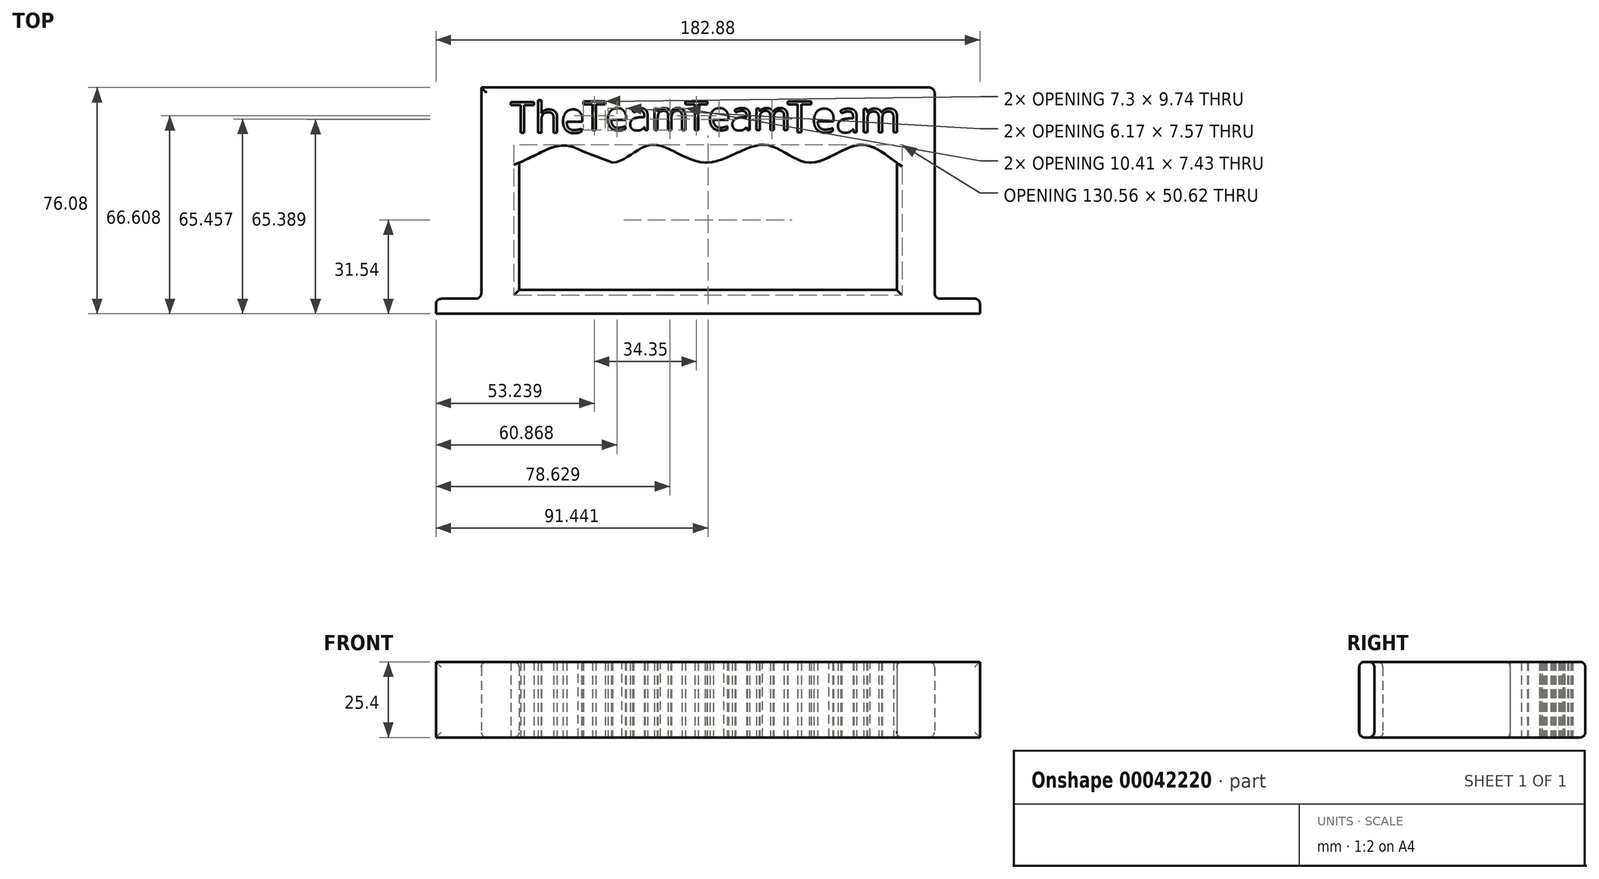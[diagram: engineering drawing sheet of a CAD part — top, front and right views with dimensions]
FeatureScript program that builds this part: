
annotation { "Feature Type Name" : "Feature", "Feature Type Description" : "" }
export const myFeature = defineFeature(function(context is Context, id is Id, definition is map)
    precondition{}
    {
        {
            var Q0;
            Q0=qCreatedBy(makeId("Top.planeOp"),FACE);
            var sketch = newSketch(context, id + "F0", { "sketchPlane" : qUnion([Q0])});
            skLineSegment(sketch, "E0", {"start": v(-62.58, -21.01) * mm, "end": v(64.42, -21.01) * mm});
            skLineSegment(sketch, "E1", {"start": v(-62.58, -21.01) * mm, "end": v(-62.58, 29.79) * mm});
            skLineSegment(sketch, "E2", {"start": v(64.42, -21.01) * mm, "end": v(64.42, 29.79) * mm});
            skLineSegment(sketch, "E3", {"start": v(-32.01, 29.79) * mm, "end": v(-31.1, 29.79) * mm});
            skLineSegment(sketch, "E4", {"start": v(-62.58, 29.79) * mm, "end": v(-62.58, 55.07) * mm});
            skLineSegment(sketch, "E5", {"start": v(-62.58, 55.07) * mm, "end": v(64.42, 55.07) * mm});
            skLineSegment(sketch, "E6", {"start": v(64.42, 55.07) * mm, "end": v(64.42, 29.79) * mm});
            skLineSegment(sketch, "E7", {"start": v(-46.2, 35.5) * mm, "end": v(-31.1, 29.79) * mm});
            skFitSpline(sketch, "E8", {"points": [v(-62.58, 29.79) * mm, v(-46.2, 35.5) * mm, v(-31.1, 29.79) * mm, v(-17.79, 35.81) * mm, v(0, 29.79) * mm, v(19.89, 35.81) * mm, v(35.06, 29.79) * mm, v(51.91, 35.81) * mm, v(64.42, 29.79) * mm], "startDerivative": vector(149.24, 59.6) * mm, "endDerivative": vector(104.83, -72.99) * mm});
            skLineSegment(sketch, "E9.trimOffspring", {"start": v(0, 29.79) * mm, "end": v(0.55, 29.79) * mm});
            skLineSegment(sketch, "E10.trimOffspring", {"start": v(35.06, 29.79) * mm, "end": v(35.59, 29.79) * mm});
            skLineSegment(sketch, "E11", {"start": v(-62.58, 55.07) * mm, "end": v(-75.28, 55.07) * mm});
            skLineSegment(sketch, "E12", {"start": v(-75.28, 55.07) * mm, "end": v(-75.28, -21.01) * mm});
            skLineSegment(sketch, "E13", {"start": v(-75.28, -21.01) * mm, "end": v(-62.58, -21.01) * mm});
            skLineSegment(sketch, "E14", {"start": v(64.42, 55.07) * mm, "end": v(77.12, 55.07) * mm});
            skLineSegment(sketch, "E15", {"start": v(77.12, 55.07) * mm, "end": v(77.12, -20.98) * mm});
            skLineSegment(sketch, "E16", {"start": v(77.12, -20.98) * mm, "end": v(64.42, -21.01) * mm});
            skLineSegment(sketch, "E17", {"start": v(-62.58, -13) * mm, "end": v(64.42, -13) * mm});
            skLineSegment(sketch, "E18", {"start": v(-75.28, -21.01) * mm, "end": v(-90.52, -21.01) * mm});
            skLineSegment(sketch, "E19", {"start": v(-90.52, -21.01) * mm, "end": v(-90.52, -15.93) * mm});
            skLineSegment(sketch, "E20", {"start": v(-90.52, -15.93) * mm, "end": v(-75.28, -15.93) * mm});
            skLineSegment(sketch, "E21", {"start": v(77.12, -20.98) * mm, "end": v(92.36, -20.98) * mm});
            skLineSegment(sketch, "E22", {"start": v(92.36, -20.98) * mm, "end": v(92.36, -15.9) * mm});
            skLineSegment(sketch, "E23", {"start": v(92.36, -15.9) * mm, "end": v(77.12, -15.9) * mm});
            skText(sketch, "E24", { "text": "The", "fontName": "OpenSans-Regular.ttf"});
            skText(sketch, "E25", { "text": "Team\n", "fontName": "OpenSans-Regular.ttf"});
            skText(sketch, "E26", { "text": "Team", "fontName": "OpenSans-Regular.ttf"});
            skText(sketch, "E27", { "text": "Team", "fontName": "OpenSans-Regular.ttf"});
            const initialGuessF0  = {"E24": [-0.06546, 0.03985, 1, 0, 0.0104], "E25": [-0.04105, 0.04073, 1, 0, 0.00982], "E26": [-0.0067, 0.04073, 1, 0, 0.00982], "E27": [0.02766, 0.04002, 1, 0, 0.01053]};
            skSetInitialGuess(sketch, initialGuessF0);
            skSolve(sketch);
        }
        {
            var Q0;
            Q0 = qSketchRegion(id + "F0", true);
            extrude(context, id + "F1", {"entities" : qUnion([Q0]), "depth" : 25.4 * mm});
        }
        {
            var Q0;
            Q0=makeQuery(id+"F1.opExtrude","CAP_EDGE",EDGE,{"disambiguationData":[OSD([sQuery(id+"F0.wireOp",EDGE,"E5"),sQuery(id+"F0.wireOp",EDGE,"E11"),sQuery(id+"F0.wireOp",EDGE,"E14")])],"isStart":false});
            var Q1;
            Q1=makeQuery(id+"F1.opExtrude","CAP_EDGE",EDGE,{"disambiguationData":[OSD([sQuery(id+"F0.wireOp",EDGE,"E12")])],"isStart":false});
            var Q2;
            Q2=makeQuery(id+"F1.opExtrude","CAP_EDGE",EDGE,{"disambiguationData":[OSD([sQuery(id+"F0.wireOp",EDGE,"E20")])],"isStart":false});
            var Q3;
            Q3=makeQuery(id+"F1.opExtrude","CAP_EDGE",EDGE,{"disambiguationData":[OSD([sQuery(id+"F0.wireOp",EDGE,"E15")])],"isStart":false});
            var Q4;
            Q4=makeQuery(id+"F1.opExtrude","CAP_EDGE",EDGE,{"disambiguationData":[OSD([sQuery(id+"F0.wireOp",EDGE,"E23")])],"isStart":false});
            var Q5;
            Q5=makeQuery(id+"F1.opExtrude","SWEPT_EDGE",EDGE,{"disambiguationData":[OSD([sQuery(id+"F0.wireOp",EDGE,"E22"),sQuery(id+"F0.wireOp",EDGE,"E23")])]});
            var Q6;
            Q6=makeQuery(id+"F1.opExtrude","CAP_EDGE",EDGE,{"disambiguationData":[OSD([sQuery(id+"F0.wireOp",EDGE,"E23")])],"isStart":true});
            var Q7;
            Q7=makeQuery(id+"F1.opExtrude","SWEPT_EDGE",EDGE,{"disambiguationData":[OSD([sQuery(id+"F0.wireOp",EDGE,"E15"),sQuery(id+"F0.wireOp",EDGE,"E23")])]});
            var Q8;
            Q8=makeQuery(id+"F1.opExtrude","SWEPT_EDGE",EDGE,{"disambiguationData":[OSD([sQuery(id+"F0.wireOp",EDGE,"E14"),sQuery(id+"F0.wireOp",EDGE,"E15")])]});
            var Q9;
            Q9=makeQuery(id+"F1.opExtrude","CAP_EDGE",EDGE,{"disambiguationData":[OSD([sQuery(id+"F0.wireOp",EDGE,"E5"),sQuery(id+"F0.wireOp",EDGE,"E11"),sQuery(id+"F0.wireOp",EDGE,"E14")])],"isStart":true});
            var Q10;
            Q10=makeQuery(id+"F1.opExtrude","CAP_EDGE",EDGE,{"disambiguationData":[OSD([sQuery(id+"F0.wireOp",EDGE,"E17")])],"isStart":true});
            var Q11;
            Q11=makeQuery(id+"F1.opExtrude","CAP_EDGE",EDGE,{"disambiguationData":[OSD([sQuery(id+"F0.wireOp",EDGE,"E2")])],"isStart":true});
            var Q12;
            Q12=makeQuery(id+"F1.opExtrude","SWEPT_EDGE",EDGE,{"disambiguationData":[OSD([sQuery(id+"F0.wireOp",EDGE,"E19"),sQuery(id+"F0.wireOp",EDGE,"E20")])]});
            var Q13;
            Q13=makeQuery(id+"F1.opExtrude","SWEPT_EDGE",EDGE,{"disambiguationData":[OSD([sQuery(id+"F0.wireOp",EDGE,"E12"),sQuery(id+"F0.wireOp",EDGE,"E20")])]});
            var Q14;
            Q14=makeQuery(id+"F1.opExtrude","CAP_EDGE",EDGE,{"disambiguationData":[OSD([sQuery(id+"F0.wireOp",EDGE,"E20")])],"isStart":true});
            var Q15;
            Q15=makeQuery(id+"F1.opExtrude","CAP_EDGE",EDGE,{"disambiguationData":[OSD([sQuery(id+"F0.wireOp",EDGE,"E15")])],"isStart":true});
            var Q16;
            Q16=makeQuery(id+"F1.opExtrude","CAP_EDGE",EDGE,{"disambiguationData":[OSD([sQuery(id+"F0.wireOp",EDGE,"E12")])],"isStart":true});
            var Q17;
            Q17=makeQuery(id+"F1.opExtrude","CAP_EDGE",EDGE,{"disambiguationData":[OSD([sQuery(id+"F0.wireOp",EDGE,"E1")])],"isStart":true});
            var Q18;
            Q18=makeQuery(id+"F1.opExtrude","CAP_EDGE",EDGE,{"disambiguationData":[OSD([sQuery(id+"F0.wireOp",EDGE,"E1")])],"isStart":false});
            var Q19;
            Q19=makeQuery(id+"F1.opExtrude","CAP_EDGE",EDGE,{"disambiguationData":[OSD([sQuery(id+"F0.wireOp",EDGE,"E2")])],"isStart":false});
            var Q20;
            Q20=makeQuery(id+"F1.opExtrude","CAP_EDGE",EDGE,{"disambiguationData":[OSD([sQuery(id+"F0.wireOp",EDGE,"E17")])],"isStart":false});
            var Q21;
            Q21=makeQuery(id+"F1.opExtrude","CAP_EDGE",EDGE,{"disambiguationData":[OSD([sQuery(id+"F0.wireOp",EDGE,"E0"),sQuery(id+"F0.wireOp",EDGE,"E13"),sQuery(id+"F0.wireOp",EDGE,"E18")])],"isStart":false});
            var Q22;
            Q22=makeQuery(id+"F1.opExtrude","CAP_EDGE",EDGE,{"disambiguationData":[OSD([sQuery(id+"F0.wireOp",EDGE,"E16")])],"isStart":false});
            var Q23;
            Q23=makeQuery(id+"F1.opExtrude","CAP_EDGE",EDGE,{"disambiguationData":[OSD([sQuery(id+"F0.wireOp",EDGE,"E21")])],"isStart":false});
            var Q24;
            Q24=makeQuery(id+"F1.opExtrude","CAP_EDGE",EDGE,{"disambiguationData":[OSD([sQuery(id+"F0.wireOp",EDGE,"E16")])],"isStart":true});
            var Q25;
            Q25=makeQuery(id+"F1.opExtrude","CAP_EDGE",EDGE,{"disambiguationData":[OSD([sQuery(id+"F0.wireOp",EDGE,"E21")])],"isStart":true});
            var Q26;
            Q26=makeQuery(id+"F1.opExtrude","CAP_EDGE",EDGE,{"disambiguationData":[OSD([sQuery(id+"F0.wireOp",EDGE,"E0"),sQuery(id+"F0.wireOp",EDGE,"E13"),sQuery(id+"F0.wireOp",EDGE,"E18")])],"isStart":true});
            fillet(context, id + "F2", {"entities" : qUnion([Q0, Q1, Q2, Q3, Q4, Q5, Q6, Q7, Q8, Q9, Q10, Q11, Q12, Q13, Q14, Q15, Q16, Q17, Q18, Q19, Q20, Q21, Q22, Q23, Q24, Q25, Q26]), "radius" : 1.78 * mm, "tangentPropagation" : true, "allowEdgeOverflow" : false});
        }
    });
